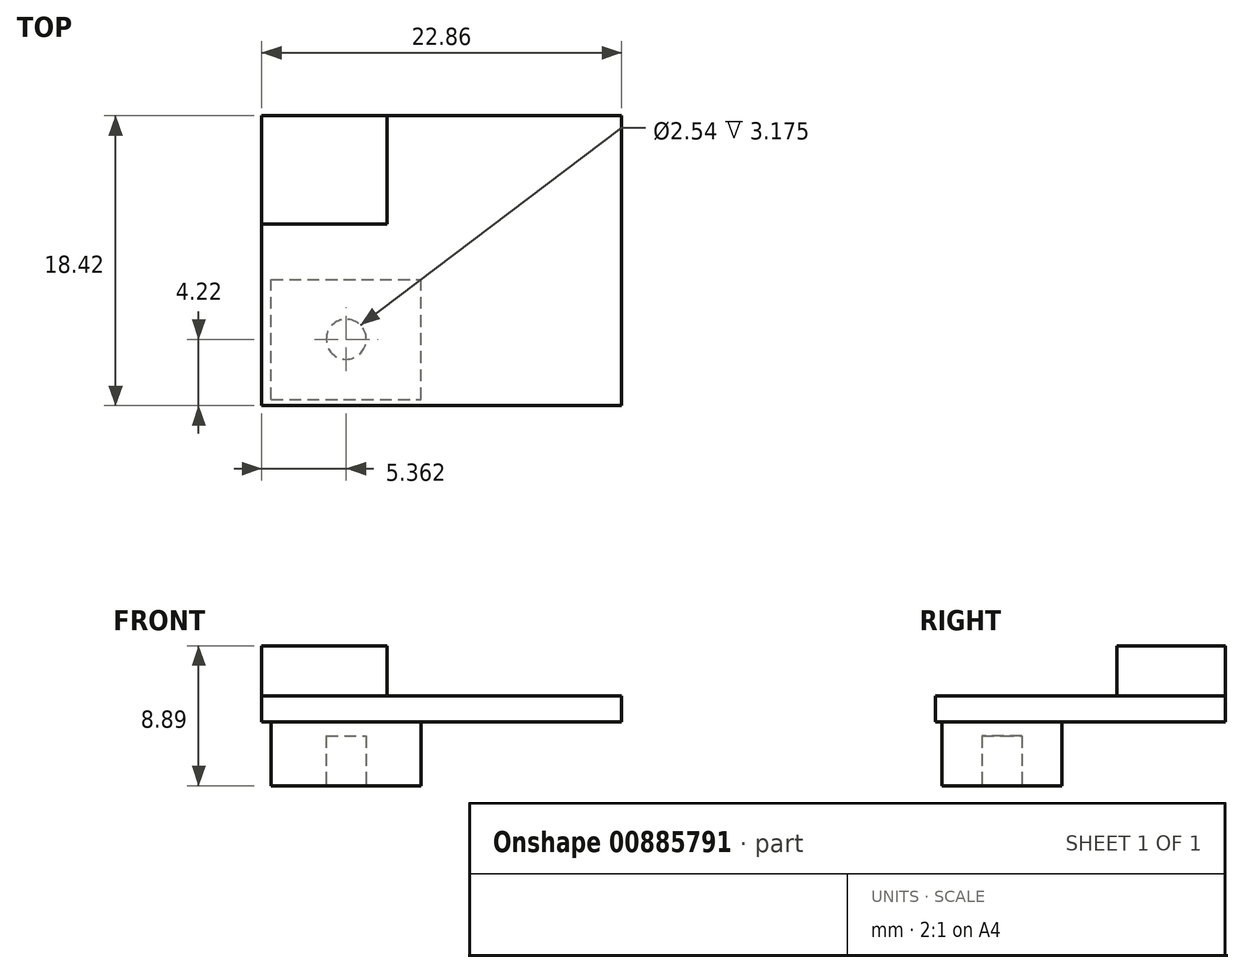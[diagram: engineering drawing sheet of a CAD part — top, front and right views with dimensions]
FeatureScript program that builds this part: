
annotation { "Feature Type Name" : "Feature", "Feature Type Description" : "" }
export const myFeature = defineFeature(function(context is Context, id is Id, definition is map)
    precondition{}
    {
        {
            var Q0;
            Q0=qCreatedBy(makeId("Top.planeOp"),FACE);
            var sketch = newSketch(context, id + "F0", { "sketchPlane" : qUnion([Q0])});
            skLineSegment(sketch, "E0.bottom", {"start": v(11.43, -9.2) * mm, "end": v(-11.43, -9.2) * mm});
            skLineSegment(sketch, "E0.top", {"start": v(11.43, 9.2) * mm, "end": v(-11.43, 9.2) * mm});
            skLineSegment(sketch, "E0.left", {"start": v(11.43, -9.2) * mm, "end": v(11.43, 9.2) * mm});
            skLineSegment(sketch, "E0.right", {"start": v(-11.43, -9.2) * mm, "end": v(-11.43, 9.2) * mm});
            skPoint(sketch, "E0.middle", {"position": v(0, 0) * mm});
            skSolve(sketch);
        }
        {
            var Q0;
            Q0 = qSketchRegion(id + "F0", true);
            extrude(context, id + "F1", {"entities" : qUnion([Q0]), "depth" : 1.65 * mm, "offsetDistance" : 25.4 * mm});
        }
        {
            var Q0;
            Q0=makeQuery(id+"F1.opExtrude","CAP_FACE",FACE,{"disambiguationData":[OSD([sQuery(id+"F0.wireOp",EDGE,"E0.bottom"),sQuery(id+"F0.wireOp",EDGE,"E0.top"),sQuery(id+"F0.wireOp",EDGE,"E0.left"),sQuery(id+"F0.wireOp",EDGE,"E0.right")])],"isStart":false});
            var sketch = newSketch(context, id + "F2", { "sketchPlane" : qUnion([Q0])});
            skLineSegment(sketch, "E1.bottom", {"start": v(-11.43, 9.2) * mm, "end": v(-3.48, 9.2) * mm});
            skLineSegment(sketch, "E1.top", {"start": v(-11.43, 2.32) * mm, "end": v(-3.48, 2.32) * mm});
            skLineSegment(sketch, "E1.left", {"start": v(-11.43, 9.2) * mm, "end": v(-11.43, 2.32) * mm});
            skLineSegment(sketch, "E1.right", {"start": v(-3.48, 9.2) * mm, "end": v(-3.48, 2.32) * mm});
            skSolve(sketch);
        }
        {
            var Q0;
            Q0=makeQuery(id+"F2.imprint","IMPRINT",FACE,{"disambiguationData":[TD([[makeQuery(id+"F2.imprint","IMPRINT",EDGE,{"derivedFrom":sQuery(id+"F2.wireOp",EDGE,"E1.bottom")}),1.0]])]});
            extrude(context, id + "F3", {"entities" : qUnion([Q0]), "operationType" : NewBodyOperationType.ADD, "depth" : 3.17 * mm, "offsetDistance" : 25.4 * mm});
        }
        {
            var Q0;
            Q0=qCreatedBy(makeId("Top.planeOp"),FACE);
            var sketch = newSketch(context, id + "F4", { "sketchPlane" : qUnion([Q0])});
            skLineSegment(sketch, "E2.bottom", {"start": v(-10.83, -8.8) * mm, "end": v(-1.3, -8.8) * mm});
            skLineSegment(sketch, "E2.top", {"start": v(-10.83, -1.18) * mm, "end": v(-1.3, -1.18) * mm});
            skLineSegment(sketch, "E2.left", {"start": v(-10.83, -8.8) * mm, "end": v(-10.83, -1.18) * mm});
            skLineSegment(sketch, "E2.right", {"start": v(-1.3, -8.8) * mm, "end": v(-1.3, -1.18) * mm});
            skSolve(sketch);
        }
        {
            var Q0;
            Q0 = qSketchRegion(id + "F4", true);
            extrude(context, id + "F5", {"entities" : qUnion([Q0]), "operationType" : NewBodyOperationType.ADD, "oppositeDirection" : true, "depth" : 4.06 * mm, "offsetDistance" : 25.4 * mm});
        }
        {
            var Q0;
            Q0=makeQuery(id+"F5.opExtrude","CAP_FACE",FACE,{"disambiguationData":[OSD([sQuery(id+"F4.wireOp",EDGE,"E2.bottom"),sQuery(id+"F4.wireOp",EDGE,"E2.top"),sQuery(id+"F4.wireOp",EDGE,"E2.left"),sQuery(id+"F4.wireOp",EDGE,"E2.right")])],"isStart":false});
            var sketch = newSketch(context, id + "F6", { "sketchPlane" : qUnion([Q0])});
            skCircle(sketch, "E3", {"center": v(-6.07, 5) * mm, "radius": 1.27 * mm});
            skPoint(sketch, "E3.centerSnap0", {"position": v(-10.83, 5) * mm});
            skPoint(sketch, "E3.centerSnap1", {"position": v(-6.07, 8.8) * mm});
            skSolve(sketch);
        }
        {
            var Q0;
            Q0 = qSketchRegion(id + "F6", true);
            extrude(context, id + "F7", {"entities" : qUnion([Q0]), "operationType" : NewBodyOperationType.REMOVE, "oppositeDirection" : true, "depth" : 3.17 * mm, "offsetDistance" : 25.4 * mm});
        }
    });
